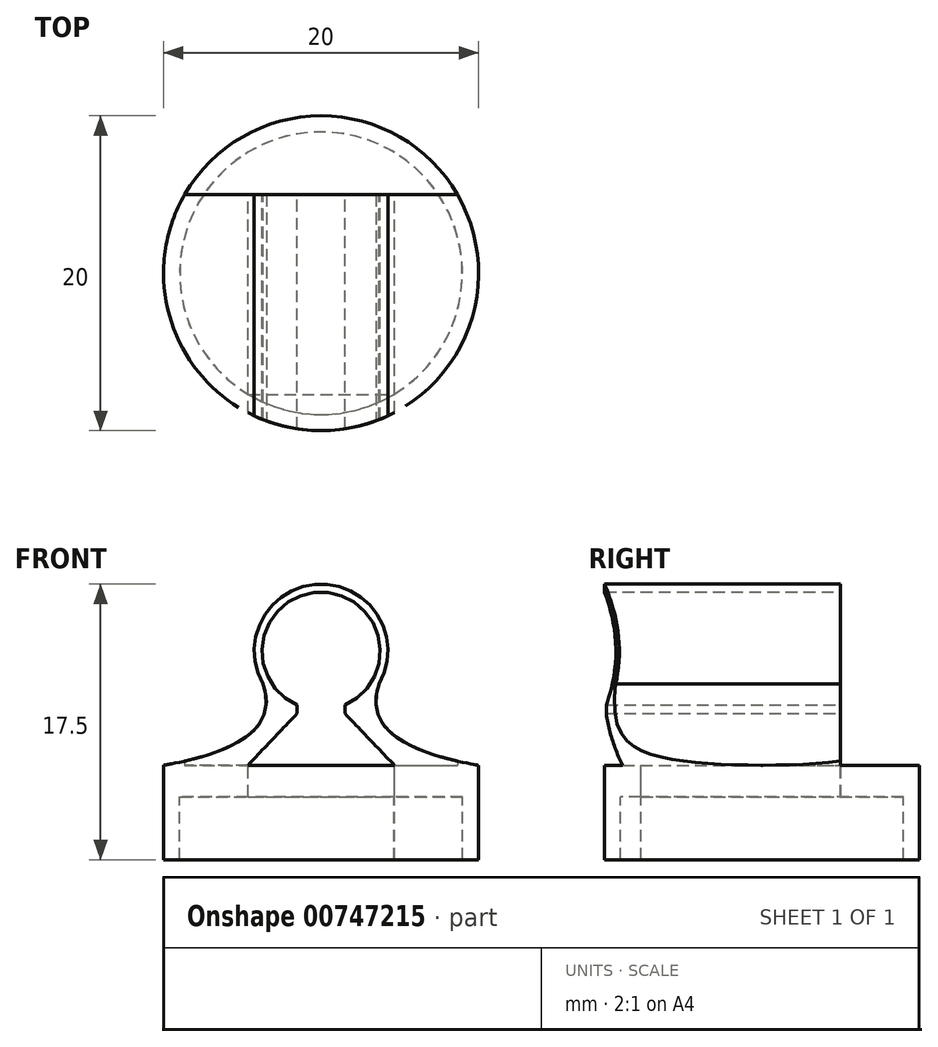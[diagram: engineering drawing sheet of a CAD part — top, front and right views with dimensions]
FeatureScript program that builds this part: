
annotation { "Feature Type Name" : "Feature", "Feature Type Description" : "" }
export const myFeature = defineFeature(function(context is Context, id is Id, definition is map)
    precondition{}
    {
        {
            var Q0;
            Q0=qCreatedBy(makeId("Front.planeOp"),FACE);
            var sketch = newSketch(context, id + "F0", { "sketchPlane" : qUnion([Q0])});
            skCircle(sketch, "E0", {"center": v(0, 2.52) * mm, "radius": 4.25 * mm});
            skCircle(sketch, "E1", {"center": v(0, 2.52) * mm, "radius": 3.75 * mm});
            skLineSegment(sketch, "E2.bottom", {"start": v(-1.5, -0.77) * mm, "end": v(1.51, -0.77) * mm});
            skLineSegment(sketch, "E2.right", {"start": v(1.51, -0.77) * mm, "end": v(1.52, -1.45) * mm});
            skFitSpline(sketch, "E3", {"points": [v(10, -4.73) * mm, v(3.7, 0.42) * mm], "startDerivative": vector(-7.48, 1.3) * mm, "endDerivative": vector(4.03, 10.74) * mm});
            skLineSegment(sketch, "E4", {"start": v(4.65, -4.73) * mm, "end": v(1.52, -1.45) * mm});
            skLineSegment(sketch, "E5", {"start": v(0, -1.73) * mm, "end": v(0, -4.35) * mm});
            skLineSegment(sketch, "E6", {"start": v(4.65, -4.73) * mm, "end": v(10, -4.73) * mm});
            skLineSegment(sketch, "E7.bottom", {"start": v(7.88, -4.73) * mm, "end": v(10.02, -4.73) * mm});
            skLineSegment(sketch, "E8.MirrorCS", {"start": v(-4.65, -4.73) * mm, "end": v(-1.52, -1.45) * mm});
            skLineSegment(sketch, "E9.MirrorCS", {"start": v(-1.51, -0.77) * mm, "end": v(-1.52, -1.45) * mm});
            skFitSpline(sketch, "E10.MirrorCS", {"points": [v(-10, -4.73) * mm, v(-3.7, 0.42) * mm], "startDerivative": vector(7.48, 1.3) * mm, "endDerivative": vector(-4.03, 10.74) * mm});
            skLineSegment(sketch, "E11.MirrorCS", {"start": v(-4.65, -4.73) * mm, "end": v(-10, -4.73) * mm});
            skLineSegment(sketch, "E12", {"start": v(-4.65, -4.73) * mm, "end": v(4.65, -4.73) * mm});
            skSolve(sketch);
        }
        {
            var Q0;
            {var subQ0=sQuery(id+"F0.wireOp",EDGE,"E0");var subQ1=makeQuery(id+"F0.imprint","INTERSECT",VERTEX,{"derivedFrom":[subQ0,sQuery(id+"F0.wireOp",EDGE,"E3")]});Q0=makeQuery(id+"F0.imprint","IMPRINT",FACE,{"disambiguationData":[TD([[makeQuery(id+"F0.imprint","IMPRINT",EDGE,{"disambiguationData":[TD([[subQ1,-1.0]])],"derivedFrom":subQ0}),1.0]])]});}
            var Q1;
            {var subQ0=sQuery(id+"F0.wireOp",EDGE,"E8.MirrorCS");Q1=makeQuery(id+"F0.imprint","IMPRINT",FACE,{"disambiguationData":[TD([[makeQuery(id+"F0.imprint","IMPRINT",EDGE,{"derivedFrom":subQ0}),1.0]])]});}
            var Q2;
            {var subQ2=sQuery(id+"F0.wireOp",EDGE,"E3");Q2=makeQuery(id+"F0.imprint","IMPRINT",FACE,{"disambiguationData":[TD([[makeQuery(id+"F0.imprint","IMPRINT",EDGE,{"derivedFrom":subQ2}),1.0]])]});}
            extrude(context, id + "F1", {"entities" : qUnion([Q0, Q1, Q2]), "depth" : 10 * mm, "offsetDistance" : 25 * mm});
        }
        {
            var Q0;
            {var subQ2=sQuery(id+"F0.wireOp",EDGE,"E3");Q0=makeQuery(id+"F0.imprint","IMPRINT",FACE,{"disambiguationData":[TD([[makeQuery(id+"F0.imprint","IMPRINT",EDGE,{"derivedFrom":subQ2}),1.0]])]});}
            var Q1;
            {var subQ0=sQuery(id+"F0.wireOp",EDGE,"E8.MirrorCS");Q1=makeQuery(id+"F0.imprint","IMPRINT",FACE,{"disambiguationData":[TD([[makeQuery(id+"F0.imprint","IMPRINT",EDGE,{"derivedFrom":subQ0}),1.0]])]});}
            var Q2;
            {var subQ0=sQuery(id+"F0.wireOp",EDGE,"E0");var subQ1=makeQuery(id+"F0.imprint","INTERSECT",VERTEX,{"derivedFrom":[subQ0,sQuery(id+"F0.wireOp",EDGE,"E3")]});Q2=makeQuery(id+"F0.imprint","IMPRINT",FACE,{"disambiguationData":[TD([[makeQuery(id+"F0.imprint","IMPRINT",EDGE,{"disambiguationData":[TD([[subQ1,-1.0]])],"derivedFrom":subQ0}),1.0]])]});}
            extrude(context, id + "F2", {"entities" : qUnion([Q0, Q1, Q2]), "operationType" : NewBodyOperationType.ADD, "oppositeDirection" : true, "depth" : 5 * mm, "offsetDistance" : 25 * mm});
        }
        {
            var Q0;
            {var subQ0=sQuery(id+"F0.wireOp",EDGE,"E7.bottom");var subQ1=sQuery(id+"F0.wireOp",EDGE,"E6");Q0=makeQuery(id+"F2.boolean.opBoolean","MERGE",FACE,{"derivedFrom":[makeQuery(id+"F1.opExtrude","SWEPT_FACE",FACE,{"disambiguationData":[OSD([subQ1,subQ0])]}),makeQuery(id+"F2.opExtrude","SWEPT_FACE",FACE,{"disambiguationData":[OSD([subQ1,subQ0])]})]});}
            var sketch = newSketch(context, id + "F3", { "sketchPlane" : qUnion([Q0])});
            skCircle(sketch, "E13", {"center": v(0, 0) * mm, "radius": 10 * mm});
            skCircle(sketch, "E14", {"center": v(0, 0) * mm, "radius": 15.36 * mm});
            skCircle(sketch, "E15", {"center": v(0, 0) * mm, "radius": 8.98 * mm});
            skLineSegment(sketch, "E16", {"start": v(-4.63, 7.69) * mm, "end": v(4.65, 7.69) * mm});
            skLineSegment(sketch, "E17", {"start": v(-4.63, 7.69) * mm, "end": v(-4.63, -5.01) * mm});
            skLineSegment(sketch, "E18", {"start": v(-4.63, -5.01) * mm, "end": v(4.65, -5) * mm});
            skLineSegment(sketch, "E19", {"start": v(4.65, -5) * mm, "end": v(4.65, 7.69) * mm});
            skSolve(sketch);
        }
        {
            var Q0;
            Q0=makeQuery(id+"F3.imprint","IMPRINT",FACE,{"disambiguationData":[TD([[makeQuery(id+"F3.imprint","IMPRINT",EDGE,{"derivedFrom":sQuery(id+"F3.wireOp",EDGE,"E14")}),1.0]])]});
            var Q1;
            {var subQ1=sQuery(id+"F0.wireOp",EDGE,"E6");var subQ5=sQuery(id+"F0.wireOp",EDGE,"E7.bottom");var subQ9=makeQuery(id+"F1.opExtrude","CAP_EDGE",EDGE,{"disambiguationData":[OSD([subQ1,subQ5])],"isStart":false});Q1=makeQuery(id+"F3.imprint","IMPRINT",FACE,{"disambiguationData":[TD([[makeQuery(id+"F3.imprint","IMPRINT",EDGE,{"derivedFrom":subQ9}),-1.0]])]});}
            var Q2;
            {var subQ0=sQuery(id+"F3.wireOp",EDGE,"E13");var subQ1=sQuery(id+"F0.wireOp",EDGE,"E7.bottom");var subQ5=makeQuery(id+"F2.opExtrude","CAP_EDGE",EDGE,{"disambiguationData":[OSD([sQuery(id+"F0.wireOp",EDGE,"E6"),subQ1])],"isStart":false});var subQ6=makeQuery(id+"F3.imprint","INTERSECT",VERTEX,{"derivedFrom":[subQ5,subQ0]});Q2=makeQuery(id+"F3.imprint","IMPRINT",FACE,{"disambiguationData":[TD([[makeQuery(id+"F3.imprint","IMPRINT",EDGE,{"disambiguationData":[TD([[subQ6,-1.0]])],"derivedFrom":subQ0}),-1.0]])]});}
            extrude(context, id + "F4", {"entities" : qUnion([Q0, Q1, Q2]), "operationType" : NewBodyOperationType.REMOVE, "oppositeDirection" : true, "depth" : 25 * mm, "offsetDistance" : 25 * mm, "hasSecondDirection" : true, "secondDirectionOppositeDirection" : false, "secondDirectionDepth" : 25 * mm});
        }
        {
            var Q0;
            {var subQ0=sQuery(id+"F3.wireOp",EDGE,"E16");var subQ6=sQuery(id+"F3.wireOp",EDGE,"E15");var subQ7=makeQuery(id+"F3.imprint","INTERSECT",VERTEX,{"derivedFrom":[subQ6,subQ0]});Q0=makeQuery(id+"F3.imprint","IMPRINT",FACE,{"disambiguationData":[TD([[makeQuery(id+"F3.imprint","IMPRINT",EDGE,{"disambiguationData":[TD([[subQ7,-1.0]])],"derivedFrom":subQ6}),-1.0]])]});}
            var Q1;
            {var subQ0=sQuery(id+"F3.wireOp",EDGE,"E17");Q1=makeQuery(id+"F3.imprint","IMPRINT",FACE,{"disambiguationData":[TD([[makeQuery(id+"F3.imprint","IMPRINT",EDGE,{"derivedFrom":subQ0}),-1.0]])]});}
            var Q2;
            {var subQ0=sQuery(id+"F3.wireOp",EDGE,"E16");var subQ1=sQuery(id+"F3.wireOp",EDGE,"E15");var subQ3=makeQuery(id+"F3.imprint","INTERSECT",VERTEX,{"derivedFrom":[subQ1,subQ0]});Q2=makeQuery(id+"F3.imprint","IMPRINT",FACE,{"disambiguationData":[TD([[makeQuery(id+"F3.imprint","IMPRINT",EDGE,{"disambiguationData":[TD([[subQ3,-1.0]])],"derivedFrom":subQ1}),1.0]])]});}
            var Q3;
            {var subQ0=sQuery(id+"F3.wireOp",EDGE,"E19");var subQ1=sQuery(id+"F3.wireOp",EDGE,"E15");var subQ2=makeQuery(id+"F3.imprint","INTERSECT",VERTEX,{"derivedFrom":[subQ1,subQ0]});Q3=makeQuery(id+"F3.imprint","IMPRINT",FACE,{"disambiguationData":[TD([[makeQuery(id+"F3.imprint","IMPRINT",EDGE,{"disambiguationData":[TD([[subQ2,1.0]])],"derivedFrom":subQ1}),1.0]])]});}
            var Q4;
            {var subQ0=sQuery(id+"F3.wireOp",EDGE,"E19");var subQ6=sQuery(id+"F3.wireOp",EDGE,"E15");var subQ7=makeQuery(id+"F3.imprint","INTERSECT",VERTEX,{"derivedFrom":[subQ6,subQ0]});Q4=makeQuery(id+"F3.imprint","IMPRINT",FACE,{"disambiguationData":[TD([[makeQuery(id+"F3.imprint","IMPRINT",EDGE,{"disambiguationData":[TD([[subQ7,1.0]])],"derivedFrom":subQ6}),-1.0]])]});}
            extrude(context, id + "F5", {"entities" : qUnion([Q0, Q1, Q2, Q3, Q4]), "operationType" : NewBodyOperationType.ADD, "depth" : 2 * mm, "offsetDistance" : 25 * mm});
        }
        {
            var Q0;
            {var subQ0=sQuery(id+"F3.wireOp",EDGE,"E13");var subQ2=sQuery(id+"F0.wireOp",EDGE,"E6");var subQ6=makeQuery(id+"F2.opExtrude","CAP_EDGE",EDGE,{"disambiguationData":[OSD([subQ2,sQuery(id+"F0.wireOp",EDGE,"E7.bottom")])],"isStart":false});var subQ7=makeQuery(id+"F3.imprint","INTERSECT",VERTEX,{"derivedFrom":[subQ6,subQ0]});Q0=makeQuery(id+"F3.imprint","IMPRINT",FACE,{"disambiguationData":[TD([[makeQuery(id+"F3.imprint","IMPRINT",EDGE,{"disambiguationData":[TD([[subQ7,1.0]])],"derivedFrom":subQ6}),-1.0]])]});}
            var Q1;
            {var subQ0=sQuery(id+"F3.wireOp",EDGE,"E13");var subQ1=sQuery(id+"F0.wireOp",EDGE,"E7.bottom");var subQ2=sQuery(id+"F0.wireOp",EDGE,"E6");var subQ3=makeQuery(id+"F2.opExtrude","CAP_EDGE",EDGE,{"disambiguationData":[OSD([subQ2,subQ1])],"isStart":false});var subQ4=makeQuery(id+"F3.imprint","INTERSECT",VERTEX,{"derivedFrom":[subQ3,subQ0]});Q1=makeQuery(id+"F3.imprint","IMPRINT",FACE,{"disambiguationData":[TD([[makeQuery(id+"F3.imprint","IMPRINT",EDGE,{"disambiguationData":[TD([[subQ4,1.0]])],"derivedFrom":subQ3}),1.0]])]});}
            extrude(context, id + "F6", {"entities" : qUnion([Q0, Q1]), "operationType" : NewBodyOperationType.ADD, "depth" : 6 * mm, "offsetDistance" : 25 * mm});
        }
    });
